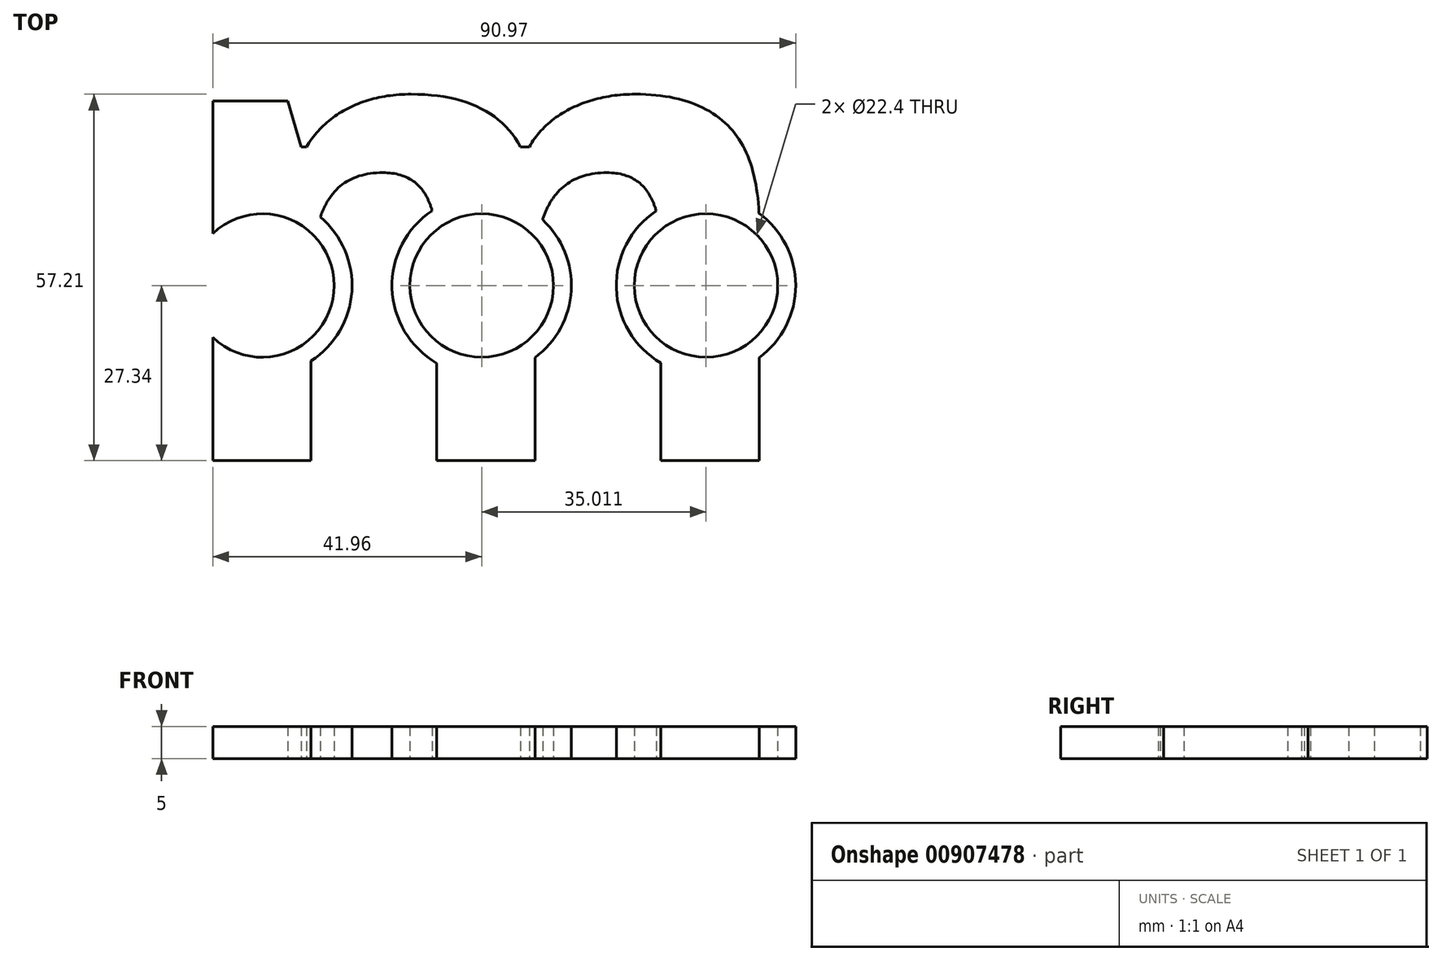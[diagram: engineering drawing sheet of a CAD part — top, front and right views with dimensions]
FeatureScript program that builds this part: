
annotation { "Feature Type Name" : "Feature", "Feature Type Description" : "" }
export const myFeature = defineFeature(function(context is Context, id is Id, definition is map)
    precondition{}
    {
        {
            var Q0;
            Q0=qCreatedBy(makeId("Top.planeOp"),FACE);
            var sketch = newSketch(context, id + "F0", { "sketchPlane" : qUnion([Q0])});
            skCircle(sketch, "E0", {"center": v(0, 0) * mm, "radius": 11.2 * mm});
            skText(sketch, "E1", { "text": "m", "fontName": "OpenSans-Bold.ttf"});
            skCircle(sketch, "E2", {"center": v(-34.23, 0) * mm, "radius": 11.2 * mm});
            skCircle(sketch, "E3", {"center": v(35.01, 0) * mm, "radius": 11.2 * mm});
            skCircle(sketch, "E4", {"center": v(-34.23, 0) * mm, "radius": 14 * mm});
            skCircle(sketch, "E5", {"center": v(0, 0) * mm, "radius": 14 * mm});
            skCircle(sketch, "E6", {"center": v(35.01, 0) * mm, "radius": 14 * mm});
            const initialGuessF0  = {"E1": [-0.05, -0.02734, 1, 0, 0.07407]};
            skSetInitialGuess(sketch, initialGuessF0);
            skSolve(sketch);
        }
        {
            var Q0;
            {var subQ19=sQuery(id+"F0.wireOp",EDGE,"E1.sketch_text.stroke-3");Q0=makeQuery(id+"F0.imprint","IMPRINT",FACE,{"disambiguationData":[TD([[makeQuery(id+"F0.imprint","IMPRINT",EDGE,{"derivedFrom":subQ19}),-1.0]])]});}
            var Q1;
            {var subQ0=sQuery(id+"F0.wireOp",EDGE,"E1.sketch_text.stroke-2");var subQ1=sQuery(id+"F0.wireOp",EDGE,"E0");var subQ2=makeQuery(id+"F0.imprint","INTERSECT",VERTEX,{"derivedFrom":[subQ1,subQ0]});Q1=makeQuery(id+"F0.imprint","IMPRINT",FACE,{"disambiguationData":[TD([[makeQuery(id+"F0.imprint","IMPRINT",EDGE,{"disambiguationData":[TD([[subQ2,-1.0]])],"derivedFrom":subQ1}),-1.0]])]});}
            var Q2;
            {var subQ0=sQuery(id+"F0.wireOp",EDGE,"E1.sketch_text.stroke-1");var subQ1=sQuery(id+"F0.wireOp",EDGE,"E0");var subQ2=makeQuery(id+"F0.imprint","INTERSECT",VERTEX,{"derivedFrom":[subQ1,subQ0]});Q2=makeQuery(id+"F0.imprint","IMPRINT",FACE,{"disambiguationData":[TD([[makeQuery(id+"F0.imprint","IMPRINT",EDGE,{"disambiguationData":[TD([[subQ2,-1.0]])],"derivedFrom":subQ1}),-1.0]])]});}
            var Q3;
            {var subQ0=sQuery(id+"F0.wireOp",EDGE,"E1.sketch_text.stroke-0");Q3=makeQuery(id+"F0.imprint","IMPRINT",FACE,{"disambiguationData":[TD([[makeQuery(id+"F0.imprint","IMPRINT",EDGE,{"derivedFrom":subQ0}),-1.0]])]});}
            var Q4;
            {var subQ0=sQuery(id+"F0.wireOp",EDGE,"E1.sketch_text.stroke-26");var subQ1=sQuery(id+"F0.wireOp",EDGE,"E0");var subQ2=makeQuery(id+"F0.imprint","INTERSECT",VERTEX,{"derivedFrom":[subQ1,subQ0]});Q4=makeQuery(id+"F0.imprint","IMPRINT",FACE,{"disambiguationData":[TD([[makeQuery(id+"F0.imprint","IMPRINT",EDGE,{"disambiguationData":[TD([[subQ2,1.0]])],"derivedFrom":subQ1}),-1.0]])]});}
            var Q5;
            {var subQ0=sQuery(id+"F0.wireOp",EDGE,"E1.sketch_text.stroke-2");var subQ1=sQuery(id+"F0.wireOp",EDGE,"E0");var subQ2=makeQuery(id+"F0.imprint","INTERSECT",VERTEX,{"derivedFrom":[subQ1,subQ0]});Q5=makeQuery(id+"F0.imprint","IMPRINT",FACE,{"disambiguationData":[TD([[makeQuery(id+"F0.imprint","IMPRINT",EDGE,{"disambiguationData":[TD([[subQ2,1.0]])],"derivedFrom":subQ1}),-1.0]])]});}
            var Q6;
            {var subQ0=sQuery(id+"F0.wireOp",EDGE,"E4");var subQ1=sQuery(id+"F0.wireOp",EDGE,"E1.sketch_text.stroke-5");var subQ2=makeQuery(id+"F0.imprint","INTERSECT",VERTEX,{"derivedFrom":[subQ1,subQ0]});Q6=makeQuery(id+"F0.imprint","IMPRINT",FACE,{"disambiguationData":[TD([[makeQuery(id+"F0.imprint","IMPRINT",EDGE,{"disambiguationData":[TD([[subQ2,-1.0]])],"derivedFrom":subQ1}),-1.0]])]});}
            var Q7;
            {var subQ0=sQuery(id+"F0.wireOp",EDGE,"E4");var subQ1=sQuery(id+"F0.wireOp",EDGE,"E1.sketch_text.stroke-5");var subQ2=makeQuery(id+"F0.imprint","INTERSECT",VERTEX,{"derivedFrom":[subQ1,subQ0]});Q7=makeQuery(id+"F0.imprint","IMPRINT",FACE,{"disambiguationData":[TD([[makeQuery(id+"F0.imprint","IMPRINT",EDGE,{"disambiguationData":[TD([[subQ2,-1.0]])],"derivedFrom":subQ1}),1.0]])]});}
            var Q8;
            {var subQ0=sQuery(id+"F0.wireOp",EDGE,"E4");var subQ1=sQuery(id+"F0.wireOp",EDGE,"E1.sketch_text.stroke-8");var subQ2=makeQuery(id+"F0.imprint","INTERSECT",VERTEX,{"disambiguationData":[OD(0.0)],"derivedFrom":[subQ1,subQ0]});Q8=makeQuery(id+"F0.imprint","IMPRINT",FACE,{"disambiguationData":[TD([[makeQuery(id+"F0.imprint","IMPRINT",EDGE,{"disambiguationData":[TD([[subQ2,-1.0]])],"derivedFrom":subQ1}),1.0]])]});}
            var Q9;
            {var subQ0=sQuery(id+"F0.wireOp",EDGE,"E4");var subQ1=sQuery(id+"F0.wireOp",EDGE,"E1.sketch_text.stroke-6");var subQ2=makeQuery(id+"F0.imprint","INTERSECT",VERTEX,{"derivedFrom":[subQ1,subQ0]});Q9=makeQuery(id+"F0.imprint","IMPRINT",FACE,{"disambiguationData":[TD([[makeQuery(id+"F0.imprint","IMPRINT",EDGE,{"disambiguationData":[TD([[subQ2,1.0]])],"derivedFrom":subQ1}),-1.0]])]});}
            var Q10;
            {var subQ0=sQuery(id+"F0.wireOp",EDGE,"E1.sketch_text.stroke-7");Q10=makeQuery(id+"F0.imprint","IMPRINT",FACE,{"disambiguationData":[TD([[makeQuery(id+"F0.imprint","IMPRINT",EDGE,{"derivedFrom":subQ0}),-1.0]])]});}
            var Q11;
            {var subQ0=sQuery(id+"F0.wireOp",EDGE,"E6");var subQ1=sQuery(id+"F0.wireOp",EDGE,"E1.sketch_text.stroke-20");var subQ2=makeQuery(id+"F0.imprint","INTERSECT",VERTEX,{"derivedFrom":[subQ1,subQ0]});Q11=makeQuery(id+"F0.imprint","IMPRINT",FACE,{"disambiguationData":[TD([[makeQuery(id+"F0.imprint","IMPRINT",EDGE,{"disambiguationData":[TD([[subQ2,1.0]])],"derivedFrom":subQ1}),-1.0]])]});}
            var Q12;
            {var subQ0=sQuery(id+"F0.wireOp",EDGE,"E1.sketch_text.stroke-21");Q12=makeQuery(id+"F0.imprint","IMPRINT",FACE,{"disambiguationData":[TD([[makeQuery(id+"F0.imprint","IMPRINT",EDGE,{"derivedFrom":subQ0}),-1.0]])]});}
            var Q13;
            {var subQ0=sQuery(id+"F0.wireOp",EDGE,"E6");var subQ1=sQuery(id+"F0.wireOp",EDGE,"E1.sketch_text.stroke-22");var subQ2=makeQuery(id+"F0.imprint","INTERSECT",VERTEX,{"derivedFrom":[subQ1,subQ0]});Q13=makeQuery(id+"F0.imprint","IMPRINT",FACE,{"disambiguationData":[TD([[makeQuery(id+"F0.imprint","IMPRINT",EDGE,{"disambiguationData":[TD([[subQ2,-1.0]])],"derivedFrom":subQ1}),1.0]])]});}
            var Q14;
            {var subQ1=sQuery(id+"F0.wireOp",EDGE,"E1.sketch_text.stroke-20");var subQ6=sQuery(id+"F0.wireOp",EDGE,"E1.sketch_text.stroke-19");var subQ7=makeQuery(id+"F0.imprint","INTERSECT",VERTEX,{"derivedFrom":[subQ6,subQ1]});Q14=makeQuery(id+"F0.imprint","IMPRINT",FACE,{"disambiguationData":[TD([[makeQuery(id+"F0.imprint","IMPRINT",EDGE,{"disambiguationData":[TD([[subQ7,1.0]])],"derivedFrom":subQ6}),1.0]])]});}
            var Q15;
            {var subQ1=sQuery(id+"F0.wireOp",EDGE,"E1.sketch_text.stroke-20");var subQ5=sQuery(id+"F0.wireOp",EDGE,"E1.sketch_text.stroke-19");var subQ6=makeQuery(id+"F0.imprint","INTERSECT",VERTEX,{"derivedFrom":[subQ5,subQ1]});Q15=makeQuery(id+"F0.imprint","IMPRINT",FACE,{"disambiguationData":[TD([[makeQuery(id+"F0.imprint","IMPRINT",EDGE,{"disambiguationData":[TD([[subQ6,1.0]])],"derivedFrom":subQ5}),-1.0]])]});}
            extrude(context, id + "F1", {"entities" : qUnion([Q0, Q1, Q2, Q3, Q4, Q5, Q6, Q7, Q8, Q9, Q10, Q11, Q12, Q13, Q14, Q15]), "depth" : 5 * mm, "offsetDistance" : 25 * mm});
        }
    });
